# Revit family: NBS_DudleyIndustriesLimited_BthrmCbnts_ModuloSlimlineBehindTheMirrorHandHygieneSystemCabinet_92406BK-1200mm
name_source: partatom
category: Casework
units: mm (PartAtom-declared; Revit-internal decimal feet)

## family parameters
Cut with Voids When Loaded = No
Host = Face
Room Calculation Point = No
Shared = No

## types (1)
- 92406BK Modulo Slimline Cabinet 1200 mm
    AssetType = Fixed
    BIMObjectName = NBS_DudleyIndustriesLimited_BathroomCabinets_ModuloSlimlineBehindTheMirrorHandHygieneSystemCabinet_92406BK-1200mm
    BlankingPlates = Not required.,Required
    CabinetDepth = 234 mm
    CabinetDoorVisible = Yes
    CabinetHeight = 960 mm  [stored 3.14961 ft]
    CabinetMaterial = NBS_DudleyIndustriesLimited_StainlessSteel_MatteBlackPowderCoated
    CabinetWidth = 1200 mm
    CarcassFinishAndColour = Matte black, powder coated
    CarcassMaterials = Stainless steel
    Category = Pr_40_30_87_03:Bathroom cabinets
    Color = Black
    Default Elevation = 1219 mm
    Description = Bathroom cabinet
    DoorsArrangement = Horizontal, top hung
    DoorsEdges = Square
    DoorsFinishAndColour = Mirrored
    DoorsHandles = Concealed
    DoorsHinges = Gas struts ensuring easy opening
    DoorsMaterial = Glass, mirrored to exterior
    DurationUnit = year
    Finish = Powder coated
    Form = Wall mounted
    IfcExportAs = IfcFurnitureType
    IfcExportType = NOTDEFINED
    IntegralAccessories = Integrated fixings
    ManufacturerName = Dudley Industries Limited
    ManufacturerURL = www.dudleyindustries.com
    Material = Stainless steel
    ModelReference = 92406BK Modulo Slimline Cabinet 1200 mm
    NBSCertification = www.nationalbimlibrary.com/cert/bnfoddsb
    Name = BathroomCabinets_ModuloSlimlineBehindTheMirrorHandHygieneSystem, Cabinet_92406BK-1200mm_DudleyIndustriesLimited
    NominalHeight = 960 mm  [stored 3.14961 ft]
    NominalLength = 0 mm  [stored 0 ft]
    NominalWidth = 1200 mm
    Shape = Rectangle
    Size = 1200 x 960 x 230 mm
    SizeNominal = 1200 x 960 x 230 mm
    Uniclass2015Code = Pr_40_30_87_03
    Uniclass2015Title = Bathroom cabinets
    Uniclass2015Version = Products v1.22
    Version = 1
    WarrantyDescription = Ten year
    WarrantyDurationParts = Ten year
    WarrantyDurationUnit = year

note: [stored X ft] marks values corroborated as IEEE doubles in the binary element streams (Revit-internal decimal feet)

## geometry (parser evidence)
native form markers: Sweep x2
no freeform markers — native parametric forms only
